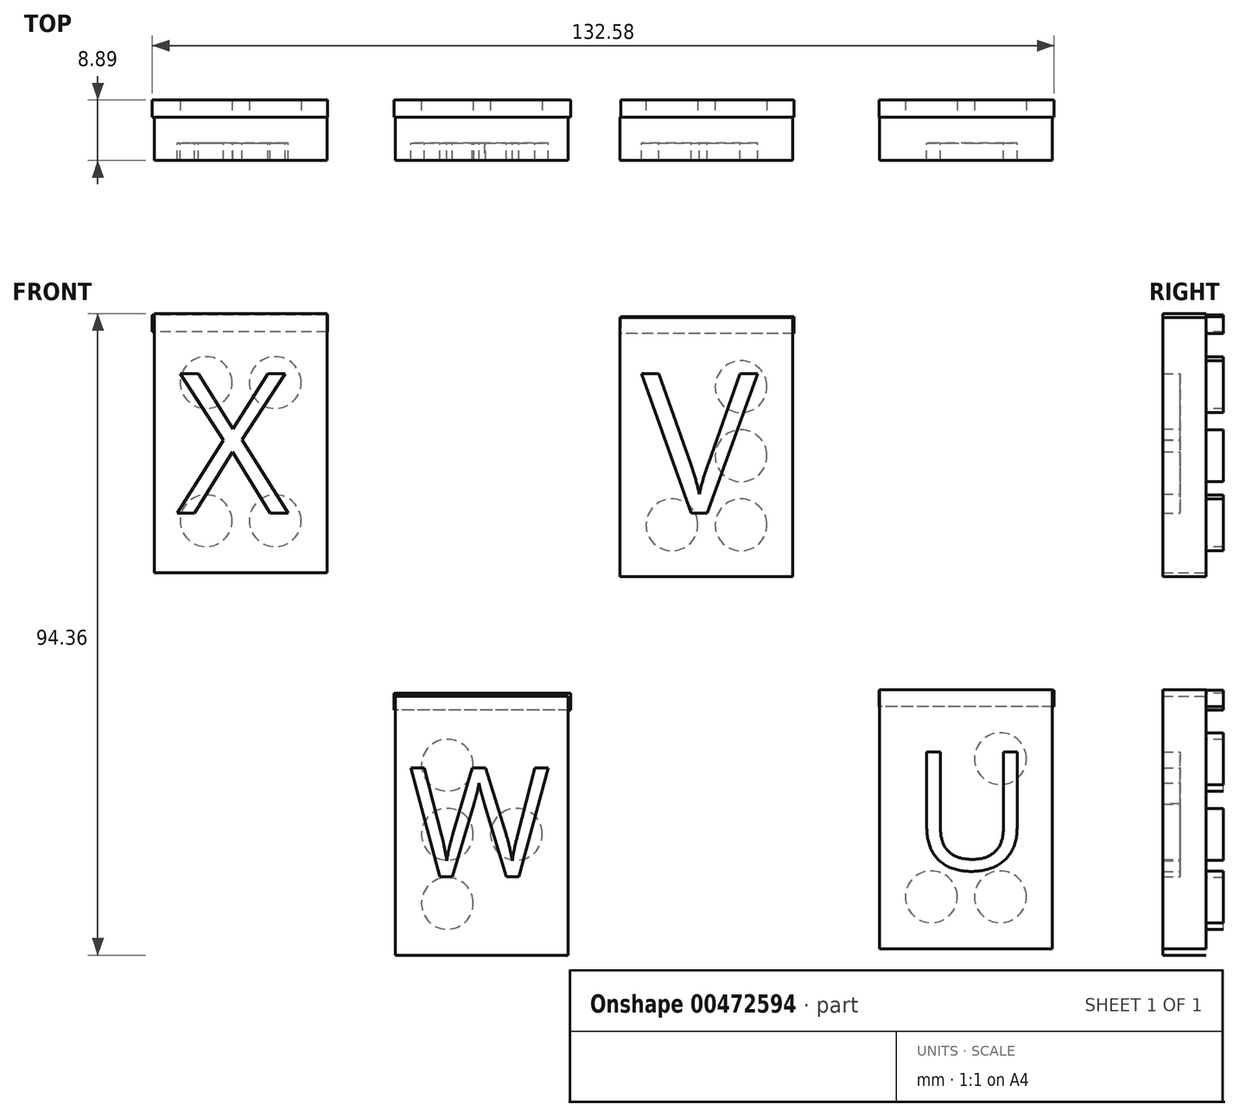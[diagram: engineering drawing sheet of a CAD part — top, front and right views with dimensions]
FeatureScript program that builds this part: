
annotation { "Feature Type Name" : "Feature", "Feature Type Description" : "" }
export const myFeature = defineFeature(function(context is Context, id is Id, definition is map)
    precondition{}
    {
        {
            var Q0;
            Q0=qCreatedBy(makeId("Front.planeOp"),FACE);
            var sketch = newSketch(context, id + "F0", { "sketchPlane" : qUnion([Q0])});
            skLineSegment(sketch, "E0.bottom", {"start": v(-58.76, 38.35) * mm, "end": v(-33.36, 38.35) * mm});
            skLineSegment(sketch, "E0.top", {"start": v(-58.76, 0.25) * mm, "end": v(-33.36, 0.25) * mm});
            skLineSegment(sketch, "E0.left", {"start": v(-58.76, 38.35) * mm, "end": v(-58.76, 0.25) * mm});
            skLineSegment(sketch, "E0.right", {"start": v(-33.36, 38.35) * mm, "end": v(-33.36, 0.25) * mm});
            skLineSegment(sketch, "E1.bottom", {"start": v(-23.3, -17.91) * mm, "end": v(2.1, -17.91) * mm});
            skLineSegment(sketch, "E1.top", {"start": v(-23.3, -56.01) * mm, "end": v(2.1, -56.01) * mm});
            skLineSegment(sketch, "E1.left", {"start": v(-23.3, -17.91) * mm, "end": v(-23.3, -56.01) * mm});
            skLineSegment(sketch, "E1.right", {"start": v(2.1, -17.91) * mm, "end": v(2.1, -56.01) * mm});
            skLineSegment(sketch, "E2.bottom", {"start": v(47.85, -16.96) * mm, "end": v(73.25, -16.96) * mm});
            skLineSegment(sketch, "E2.top", {"start": v(47.85, -55.06) * mm, "end": v(73.25, -55.06) * mm});
            skLineSegment(sketch, "E2.left", {"start": v(47.85, -16.96) * mm, "end": v(47.85, -55.06) * mm});
            skLineSegment(sketch, "E2.right", {"start": v(73.25, -16.96) * mm, "end": v(73.25, -55.06) * mm});
            skLineSegment(sketch, "E3.bottom", {"start": v(9.7, 37.75) * mm, "end": v(35.1, 37.75) * mm});
            skLineSegment(sketch, "E3.top", {"start": v(9.7, -0.35) * mm, "end": v(35.1, -0.35) * mm});
            skLineSegment(sketch, "E3.left", {"start": v(9.7, 37.75) * mm, "end": v(9.7, -0.35) * mm});
            skLineSegment(sketch, "E3.right", {"start": v(35.1, 37.75) * mm, "end": v(35.1, -0.35) * mm});
            skSolve(sketch);
        }
        {
            var Q0;
            Q0 = qSketchRegion(id + "F0", true);
            extrude(context, id + "F1", {"entities" : qUnion([Q0]), "depth" : 6.35 * mm});
        }
        {
            var Q0;
            Q0=qCreatedBy(makeId("Front.planeOp"),FACE);
            var sketch = newSketch(context, id + "F2", { "sketchPlane" : qUnion([Q0])});
            skCircle(sketch, "E4", {"center": v(27.49, 7.27) * mm, "radius": 3.81 * mm});
            skCircle(sketch, "E5", {"center": v(27.49, 17.43) * mm, "radius": 3.81 * mm});
            skCircle(sketch, "E6", {"center": v(65.63, -27.12) * mm, "radius": 3.81 * mm});
            skCircle(sketch, "E7", {"center": v(65.63, -47.44) * mm, "radius": 3.81 * mm});
            skCircle(sketch, "E8", {"center": v(-5.52, -38.23) * mm, "radius": 3.81 * mm});
            skCircle(sketch, "E9", {"center": v(-15.68, -28.07) * mm, "radius": 3.81 * mm});
            skCircle(sketch, "E10", {"center": v(27.49, 27.59) * mm, "radius": 3.81 * mm});
            skCircle(sketch, "E11", {"center": v(17.33, 7.27) * mm, "radius": 3.81 * mm});
            skCircle(sketch, "E12", {"center": v(-15.68, -48.4) * mm, "radius": 3.8 * mm});
            skCircle(sketch, "E13", {"center": v(-40.98, 28.19) * mm, "radius": 3.81 * mm});
            skCircle(sketch, "E14", {"center": v(-51.14, 28.19) * mm, "radius": 3.81 * mm});
            skCircle(sketch, "E15", {"center": v(-51.14, 7.87) * mm, "radius": 3.81 * mm});
            skCircle(sketch, "E16", {"center": v(-40.98, 7.87) * mm, "radius": 3.81 * mm});
            skCircle(sketch, "E17", {"center": v(55.47, -47.44) * mm, "radius": 3.81 * mm});
            skCircle(sketch, "E18", {"center": v(-15.68, -38.23) * mm, "radius": 3.81 * mm});
            skSolve(sketch);
        }
        {
            var Q0;
            Q0 = qSketchRegion(id + "F2", true);
            extrude(context, id + "F3", {"entities" : qUnion([Q0]), "operationType" : NewBodyOperationType.ADD, "oppositeDirection" : true, "depth" : 2.54 * mm});
        }
        {
            var Q0;
            Q0=qCreatedBy(makeId("Front.planeOp"),FACE);
            cPlane(context, id + "F4", {"entities" : qUnion([Q0]), "cplaneType" : CPlaneType.OFFSET, "offset" : 3.8 * mm, "width" : 152.4 * mm, "height" : 152.4 * mm});
        }
        {
            var Q0;
            Q0=qCreatedBy(id+"F4.planeOp",FACE);
            var sketch = newSketch(context, id + "F5", { "sketchPlane" : qUnion([Q0])});
            skText(sketch, "E19", { "text": "U", "fontName": "OpenSans-Regular.ttf"});
            skText(sketch, "E20", { "text": "V", "fontName": "OpenSans-Regular.ttf"});
            skText(sketch, "E21", { "text": "W", "fontName": "OpenSans-Regular.ttf"});
            skText(sketch, "E22", { "text": "X", "fontName": "OpenSans-Regular.ttf"});
            const initialGuessF5  = {"E19": [0.0526, -0.04345, 1, 0, 0.01749], "E20": [0.01285, 0.009, 1, 0, 0.02066], "E21": [-0.02133, -0.0445, 1, 0, 0.01616], "E22": [-0.0555, 0.009, 1, 0, 0.02066]};
            skSetInitialGuess(sketch, initialGuessF5);
            skSolve(sketch);
        }
        {
            var Q0;
            Q0 = qSketchRegion(id + "F5", true);
            extrude(context, id + "F6", {"entities" : qUnion([Q0]), "operationType" : NewBodyOperationType.REMOVE, "depth" : 25.4 * mm});
        }
        {
            var Q0;
            Q0=qCreatedBy(makeId("Front.planeOp"),FACE);
            var sketch = newSketch(context, id + "F7", { "sketchPlane" : qUnion([Q0])});
            skLineSegment(sketch, "E23.bottom", {"start": v(73.52, -17.03) * mm, "end": v(47.79, -17.03) * mm});
            skLineSegment(sketch, "E23.top", {"start": v(73.52, -19.48) * mm, "end": v(47.79, -19.48) * mm});
            skLineSegment(sketch, "E23.left", {"start": v(73.52, -17.03) * mm, "end": v(73.52, -19.48) * mm});
            skLineSegment(sketch, "E23.right", {"start": v(47.79, -17.03) * mm, "end": v(47.79, -19.48) * mm});
            skLineSegment(sketch, "E24.bottom", {"start": v(35.29, 37.86) * mm, "end": v(9.8, 37.86) * mm});
            skLineSegment(sketch, "E24.top", {"start": v(35.29, 35.41) * mm, "end": v(9.8, 35.41) * mm});
            skLineSegment(sketch, "E24.left", {"start": v(35.29, 37.86) * mm, "end": v(35.29, 35.41) * mm});
            skLineSegment(sketch, "E24.right", {"start": v(9.8, 37.86) * mm, "end": v(9.8, 35.41) * mm});
            skLineSegment(sketch, "E25.bottom", {"start": v(-33.33, 38.1) * mm, "end": v(-59.06, 38.1) * mm});
            skLineSegment(sketch, "E25.top", {"start": v(-33.33, 35.66) * mm, "end": v(-59.06, 35.66) * mm});
            skLineSegment(sketch, "E25.left", {"start": v(-33.33, 38.1) * mm, "end": v(-33.33, 35.66) * mm});
            skLineSegment(sketch, "E25.right", {"start": v(-59.06, 38.1) * mm, "end": v(-59.06, 35.66) * mm});
            skLineSegment(sketch, "E26.bottom", {"start": v(2.45, -17.52) * mm, "end": v(-23.53, -17.52) * mm});
            skLineSegment(sketch, "E26.top", {"start": v(2.45, -19.97) * mm, "end": v(-23.53, -19.97) * mm});
            skLineSegment(sketch, "E26.left", {"start": v(2.45, -17.52) * mm, "end": v(2.45, -19.97) * mm});
            skLineSegment(sketch, "E26.right", {"start": v(-23.53, -17.52) * mm, "end": v(-23.53, -19.97) * mm});
            skSolve(sketch);
        }
        {
            var Q0;
            Q0 = qSketchRegion(id + "F7", true);
            extrude(context, id + "F8", {"entities" : qUnion([Q0]), "operationType" : NewBodyOperationType.ADD, "oppositeDirection" : true, "depth" : 2.54 * mm});
        }
    });
